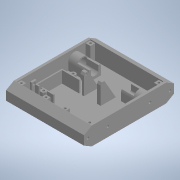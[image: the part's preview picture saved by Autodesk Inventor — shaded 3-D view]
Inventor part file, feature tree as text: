
AUTODESK INVENTOR PART (.ipt)
format: ipt  version: 2020 (Build 240168000, 168)  size: 589,824 bytes
history: native  units: in
note: dims shown in document units (in); Inventor stores cm internally (conversion verified against a paired STEP export)
features: extrude x17, sketch x16, projected_geometry x14, mirror x6, plane x1
ambient origin geometry x8: Origin, YZ Plane, XZ Plane, XY Plane, X Axis, Y Axis, Z Axis, Center Point
bodies: Solid1 (feature_tree)
feature tree (54):
  extrude  "Extrusion1"  Depth=5.9055in
  extrude  "Extrusion2"  TaperAngle=0.0deg  [1 undecoded]
  extrude  "Extrusion3"  Depth=1.063in
  extrude  "Extrusion4"  Depth=0.315in
  extrude  "Extrusion5"  TaperAngle=0.0deg  [1 undecoded]
  extrude  "Extrusion6"  Depth=0.5906in
  mirror  "Mirror1"
  extrude  "Extrusion7"  Depth=0.0787in
  mirror  "Mirror2"
  extrude  "Extrusion8"  Depth=0.6102in
  mirror  "Mirror3"
  plane  "Work Plane1"
  extrude  "Extrusion9"  Depth=0.7874in TaperAngle=0.0deg
  mirror  "Mirror4"
  extrude  "Extrusion10"  Depth=6.063in TaperAngle=0.0deg
  extrude  "Extrusion11"  Depth=0.1575in
  extrude  "Extrusion12"  TaperAngle=0.0deg  [1 undecoded]
  extrude  "Extrusion13"  Depth=0.2756in
  extrude  "Extrusion14"  Depth=0.4331in
  extrude  "Extrusion17"  Depth=2.7559in
  extrude  "Extrusion18"  Depth=0.0394in
  mirror  "Mirror6"
  extrude  "Extrusion19"  Depth=0.2362in
  mirror  "Mirror7"
  sketch  "Sketch1"  dims[d0=1.1811in d1=5.9055in]
  sketch  "Sketch2"  dims[d2=5.1181in d3=0.0in]
  projected_geometry  "Projected Loop1"
  sketch  "Sketch3"  dims[d4=0.1575in d5=1.063in]
  projected_geometry  "Projected Loop2"
  projected_geometry  "Projected Loop3"
  sketch  "Sketch4"  dims[d6=0.0in d8=0.315in]
  projected_geometry  "Projected Loop4"
  sketch  "Sketch6"  dims[d10=0.993in d11=0.0in]
  sketch  "Sketch7"  dims[d12=0.6496in d13=0.5906in]
  sketch  "Sketch9"  dims[d14=1.5748in d15=0.0787in]
  sketch  "Sketch10"  dims[d16=0.5512in d17=0.0in d18=0.6102in]
  sketch  "Sketch12"  dims[d19=0.4803in d20=0.7874in d21=0.0in]
  projected_geometry  "Projected Loop6"
  projected_geometry  "Projected Loop7"
  projected_geometry  "Projected Loop8"
  sketch  "Sketch13"  dims[d22=0.1654in d23=6.063in d24=0.0in]
  sketch  "Sketch14"  dims[d25=0.5114in d26=0.1575in]
  sketch  "Sketch15"  dims[d27=1.5748in d28=0.0in d29=0.0in]
  projected_geometry  "Projected Loop15"
  sketch  "Sketch16"  dims[d30=0.1575in d31=0.2756in]
  projected_geometry  "Projected Loop19"
  projected_geometry  "Projected Loop20"
  projected_geometry  "Projected Loop21"
  projected_geometry  "Projected Loop22"
  projected_geometry  "Projected Loop23"
  projected_geometry  "Projected Loop24"
  sketch  "Sketch20"  dims[d32=0.0in d33=0.4331in]
  sketch  "Sketch21"  dims[d34=0.122in d38=2.7559in]
  sketch  "Sketch22"  dims[d40=0.061in d41=0.0909in d42=0.2362in d43=0.0in d44=60.0deg d45=0.0787in d46=0.315in d48=0.993in d49=0.0in d53=0.2756in d54=0.0in d55=0.4724in d56=1.2008in d57=1.6142in d58=1.5945in d59=0.0787in d60=0.0787in d62=0.315in d63=0.7677in d64=0.0in d66=0.1476in d67=0.2756in d68=0.0in d69=0.7874in d70=0.2953in d71=0.1181in d72=0.0in d89=0.0157in d90=0.0157in d91=0.1476in d92=0.1476in d96=0.315in d97=0.1575in d98=0.1181in d99=0.0in d102=0.1772in d104=0.3346in d105=135.0deg d106=0.2362in d107=0.0in d108=0.0394in d109=0.0in]
note: 3 required parameter values undecoded (feature->parameter linkage not recoverable at this tier; creation-order binding heuristic only, values carry confidence <= 0.55)
